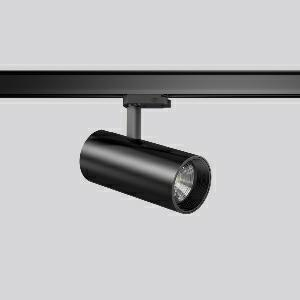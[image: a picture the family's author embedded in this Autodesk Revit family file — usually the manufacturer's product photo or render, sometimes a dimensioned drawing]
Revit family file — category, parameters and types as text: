
# Revit family: deecos_s_mini_742209_003_76_be28
name_source: partatom
category: Lighting Fixtures
units: mm (PartAtom-declared; Revit-internal decimal feet)

## family parameters
Cut with Voids When Loaded = No
Host = Face
Light Source = No
Part Type = Normal
Room Calculation Point = No
Round Connector Dimension = Use Diameter
Shared = No

## types (1)
- DEECOS S mini (1 x LED Modul 930, 3250 lm, 3000)
    Apparent Load = 29 VA
    Approval mark = CE
    CIE Flux Codes = 80 99 100 100 100
    Color Rendering = 90
    Color Temperature = 3000
    Default Elevation = 1800 mm
    Description = Series: DEECOS S mini
LED surface-mounted projector in modern design with no visible cooling ribs. Housing: die-cast aluminium, powder-coated. Rotation range: 356°. Swivel range: 90°. Black plastic ring and recessed LED to prevent glare from the side. Optical assembly with lens made of plastic (polycarbonate) for the best homogeneous light distribution - can be changed without tools. Best colour rendering index Ra>90. With adapter for RZB 3-circuit DALI tracks. Suitable for Track on ceiling, Wall track. High quality converter without flickering and stroboscopic effect. The following accessories can be mounted without use of tools: interchangeable lenses, decorative glasses, honeycomb louvre, clear and frosted diffusers, white interchangeable plastic ring. 
Colour: deep black, matt (RAL 9005)
Diameter: 87 mm
Height: 214 mm
Lamp: LED
Socket: without socket
Colour temperature: 3000K
Colour rendering index (CRI): 92
System power: 29 W
Rated luminous flux: 3250 lm
Luminous efficiency: 112 lm/W
Control gear: Converter, dimmable, DALI
Protection class: I
Type of protection: IP 20
    Height = 214 mm
    Lamp = 1 x LED Modul 930
    Lamp Light Flux = 3250 lm
    Lamp count = 1
    Length = 87 mm
    Lifetime = 50000 h
    Luminous efficacy = 112 lm/W
    Manufacturer = RZB
    ModVariant = No
    Model = 742209.003.76
    Mounting Place = Ceiling
    Mounting Type = Rail mounted
    Number of Poles = 1
    OnlyDefault = Yes
    Power Factor = 1
    Product Name = DEECOS S mini
    Product group = Track mounted projectors
    ProductGroupID = 301
    Protection Class = Protection class I
    Protection Degree = IP 20
    RLX_Detail_Level = 1
    RLX_Emergency_Light_Flux = 0 lm
    RLX_Emergency_Type = 0
    RLX_Emergency_Type_DB = No
    RlxData = <blob elided: 38605 chars, md5=7a07cc3f>
    Socket = socket
    Standby Power = 0 W
    System Light Flux = 3250 lm
    System Power = 29 W
    Type Comments = Product without accessories
    Type Image = 741930.003.jpg
    URL = http://relux.com
    VarID = ---
    Voltage = 230 V
    Voltage Range = 220-240 V
    Weight = 0.00 kg
    Width = 0 mm  [stored 0 ft]

note: [stored X ft] marks values corroborated as IEEE doubles in the binary element streams (Revit-internal decimal feet)

## geometry (parser evidence)
native form markers: Blend x4, Sweep x12
no freeform markers — native parametric forms only
